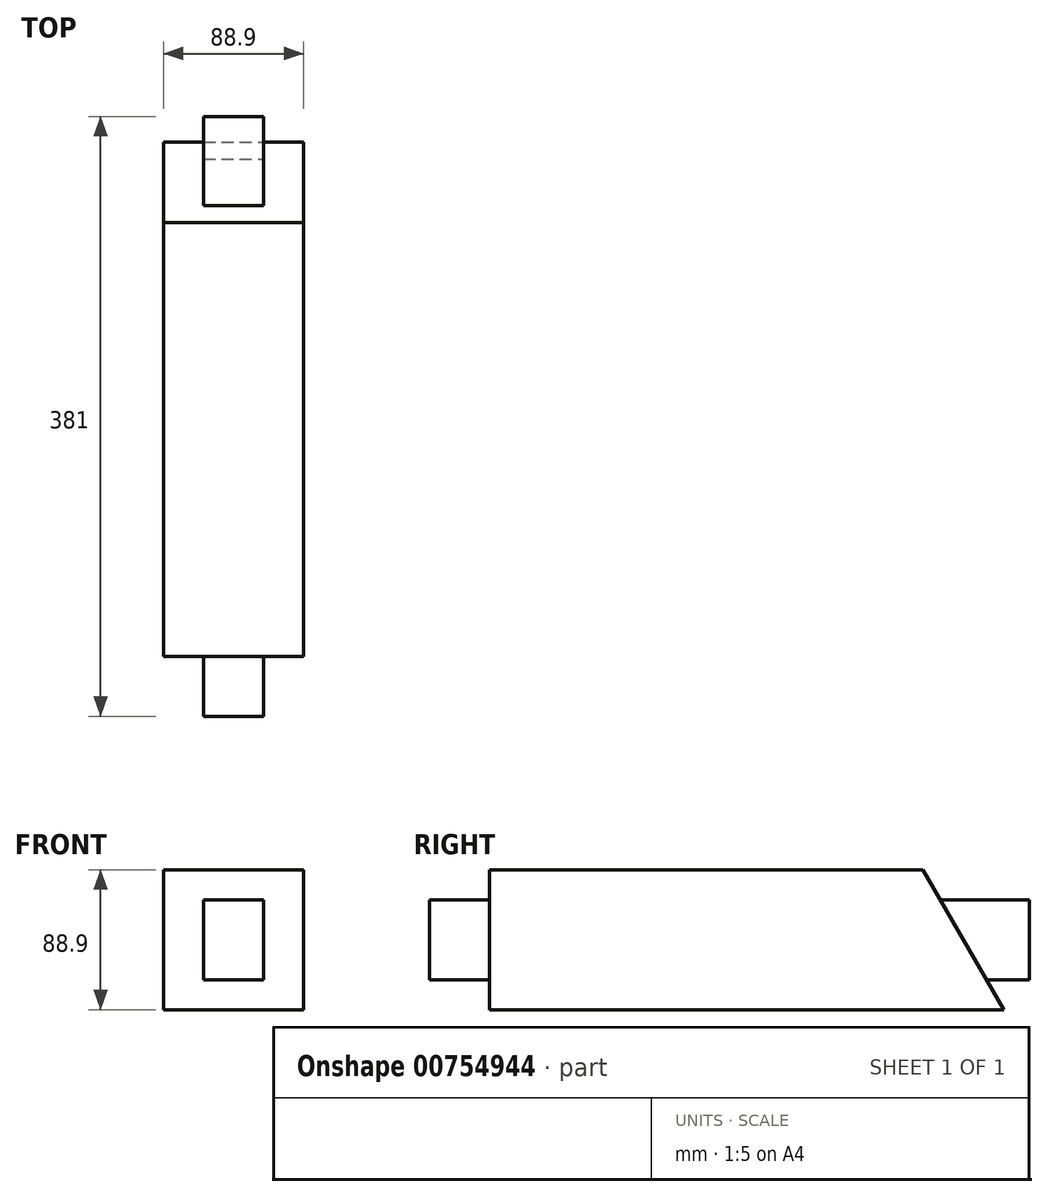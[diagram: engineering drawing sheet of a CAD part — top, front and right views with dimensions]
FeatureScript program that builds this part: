
annotation { "Feature Type Name" : "Feature", "Feature Type Description" : "" }
export const myFeature = defineFeature(function(context is Context, id is Id, definition is map)
    precondition{}
    {
        {
            var Q0;
            Q0=qCreatedBy(makeId("Right.planeOp"),FACE);
            var sketch = newSketch(context, id + "F0", { "sketchPlane" : qUnion([Q0])});
            skLineSegment(sketch, "E0.bottom", {"start": v(-190.5, 44.45) * mm, "end": v(190.5, 44.45) * mm});
            skLineSegment(sketch, "E0.top", {"start": v(-190.5, -44.45) * mm, "end": v(190.5, -44.45) * mm});
            skLineSegment(sketch, "E0.left", {"start": v(-190.5, 44.45) * mm, "end": v(-190.5, -44.45) * mm});
            skLineSegment(sketch, "E0.right", {"start": v(190.5, 44.45) * mm, "end": v(190.5, -44.45) * mm});
            skPoint(sketch, "E0.middle", {"position": v(0, 0) * mm});
            skSolve(sketch);
        }
        {
            var Q0;
            Q0 = qSketchRegion(id + "F0", true);
            extrude(context, id + "F1", {"entities" : qUnion([Q0]), "endBound" : BoundingType.SYMMETRIC, "depth" : 88.9 * mm, "offsetDistance" : 25.4 * mm});
        }
        {
            var Q0;
            Q0=makeQuery(id+"F1.opExtrude","SWEPT_FACE",FACE,{"disambiguationData":[OSD([sQuery(id+"F0.wireOp",EDGE,"E0.bottom")])]});
            var sketch = newSketch(context, id + "F2", { "sketchPlane" : qUnion([Q0])});
            skLineSegment(sketch, "E1", {"start": v(-44.45, 122.94) * mm, "end": v(44.45, 122.94) * mm, "construction": true});
            skSolve(sketch);
        }
        {
            var Q0;
            Q0=sQuery(id+"F2.wireOp",EDGE,"E1");
            cPlane(context, id + "F3", {"entities" : qUnion([Q0]), "cplaneType" : CPlaneType.LINE_ANGLE, "offset" : 25.4 * mm, "angle" : 30 * degree, "width" : 152.4 * mm, "height" : 152.4 * mm});
        }
        {
            var Q0;
            Q0=makeQuery(id+"F1.opExtrude","SWEPT_FACE",FACE,{"disambiguationData":[OSD([sQuery(id+"F0.wireOp",EDGE,"E0.right")])]});
            var sketch = newSketch(context, id + "F4", { "sketchPlane" : qUnion([Q0])});
            skLineSegment(sketch, "E2.bottom", {"start": v(-44.45, 44.45) * mm, "end": v(44.45, 44.45) * mm});
            skLineSegment(sketch, "E2.top", {"start": v(-44.45, -44.45) * mm, "end": v(44.45, -44.45) * mm});
            skLineSegment(sketch, "E2.left", {"start": v(-44.45, 44.45) * mm, "end": v(-44.45, -44.45) * mm});
            skLineSegment(sketch, "E2.right", {"start": v(44.45, 44.45) * mm, "end": v(44.45, -44.45) * mm});
            skPoint(sketch, "E2.middle", {"position": v(0, 0) * mm});
            skLineSegment(sketch, "E3.bottom", {"start": v(-19.05, 25.4) * mm, "end": v(19.05, 25.4) * mm});
            skLineSegment(sketch, "E3.top", {"start": v(-19.05, -25.4) * mm, "end": v(19.05, -25.4) * mm});
            skLineSegment(sketch, "E3.left", {"start": v(-19.05, 25.4) * mm, "end": v(-19.05, -25.4) * mm});
            skLineSegment(sketch, "E3.right", {"start": v(19.05, 25.4) * mm, "end": v(19.05, -25.4) * mm});
            skSolve(sketch);
        }
        {
            var Q0;
            Q0 = qSketchRegion(id + "F4", true);
            var Q1;
            Q1=qCreatedBy(id+"F3.planeOp",FACE);
            extrude(context, id + "F5", {"entities" : qUnion([Q0]), "operationType" : NewBodyOperationType.REMOVE, "endBound" : BoundingType.UP_TO_SURFACE, "oppositeDirection" : true, "depth" : 25.4 * mm, "endBoundEntityFace" : qUnion([Q1]), "offsetDistance" : 25.4 * mm});
        }
        {
            var Q0;
            Q0=makeQuery(id+"F1.opExtrude","SWEPT_FACE",FACE,{"disambiguationData":[OSD([sQuery(id+"F0.wireOp",EDGE,"E0.left")])]});
            var sketch = newSketch(context, id + "F6", { "sketchPlane" : qUnion([Q0])});
            skLineSegment(sketch, "E4.bottom", {"start": v(-44.45, 44.45) * mm, "end": v(44.45, 44.45) * mm});
            skLineSegment(sketch, "E4.top", {"start": v(-44.45, -44.45) * mm, "end": v(44.45, -44.45) * mm});
            skLineSegment(sketch, "E4.left", {"start": v(-44.45, 44.45) * mm, "end": v(-44.45, -44.45) * mm});
            skLineSegment(sketch, "E4.right", {"start": v(44.45, 44.45) * mm, "end": v(44.45, -44.45) * mm});
            skPoint(sketch, "E4.middle", {"position": v(0, 0) * mm});
            skLineSegment(sketch, "E5.bottom", {"start": v(-19.05, 25.4) * mm, "end": v(19.05, 25.4) * mm});
            skLineSegment(sketch, "E5.top", {"start": v(-19.05, -25.4) * mm, "end": v(19.05, -25.4) * mm});
            skLineSegment(sketch, "E5.left", {"start": v(-19.05, 25.4) * mm, "end": v(-19.05, -25.4) * mm});
            skLineSegment(sketch, "E5.right", {"start": v(19.05, 25.4) * mm, "end": v(19.05, -25.4) * mm});
            skSolve(sketch);
        }
        {
            var Q0;
            Q0 = qSketchRegion(id + "F6", true);
            extrude(context, id + "F7", {"entities" : qUnion([Q0]), "operationType" : NewBodyOperationType.REMOVE, "oppositeDirection" : true, "depth" : 38.1 * mm, "offsetDistance" : 25.4 * mm});
        }
    });
